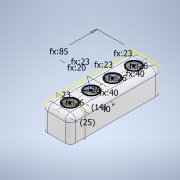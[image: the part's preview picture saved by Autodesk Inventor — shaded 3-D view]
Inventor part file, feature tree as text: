
AUTODESK INVENTOR PART (.ipt)
format: ipt  version: 2021 (Build 250183000, 183)  size: 2,158,592 bytes
history: native  units: in
note: dims shown in document units (in); Inventor stores cm internally (conversion verified against a paired STEP export)
features: extrude x9, other x9, fillet x2
ambient origin geometry x8: Origin, YZ Plane, XZ Plane, XY Plane, X Axis, Y Axis, Z Axis, Center Point
bodies: Body1 (feature_tree)
feature tree (20):
  extrude  "Base"  Depth=6.6929in
  other  "Top Indent Sketch"
  extrude  "Top"  Depth=2.0472in
  extrude  "Walls"  Depth=1.7717in TaperAngle=0.0deg
  fillet  "Outer"  Radius=1.0236in
  extrude  "Outer Wire"  Depth=1.0236in
  extrude  "Wall Holes"  Depth=1.0236in
  extrude  "Text"  Depth=1.0236in
  extrude  "Inner Sketch"  Depth=1.5748in
  fillet  "Inner Fillet"  Radius=1.5748in
  extrude  "Top Indent"  Depth=1.5748in
  other  "Wire Hole Plane"
  extrude  "Wire Hole"  Depth=0.7087in TaperAngle=0.0deg
  other  "Base Sketch"
  other  "Walls Sketch"
  other  "Outer Wire Sketch"
  other  "Wall Holes Sketch"
  other  "Text Sketch"
  other  "Inner Support Sketch"
  other  "Wire Hole Sketch"
